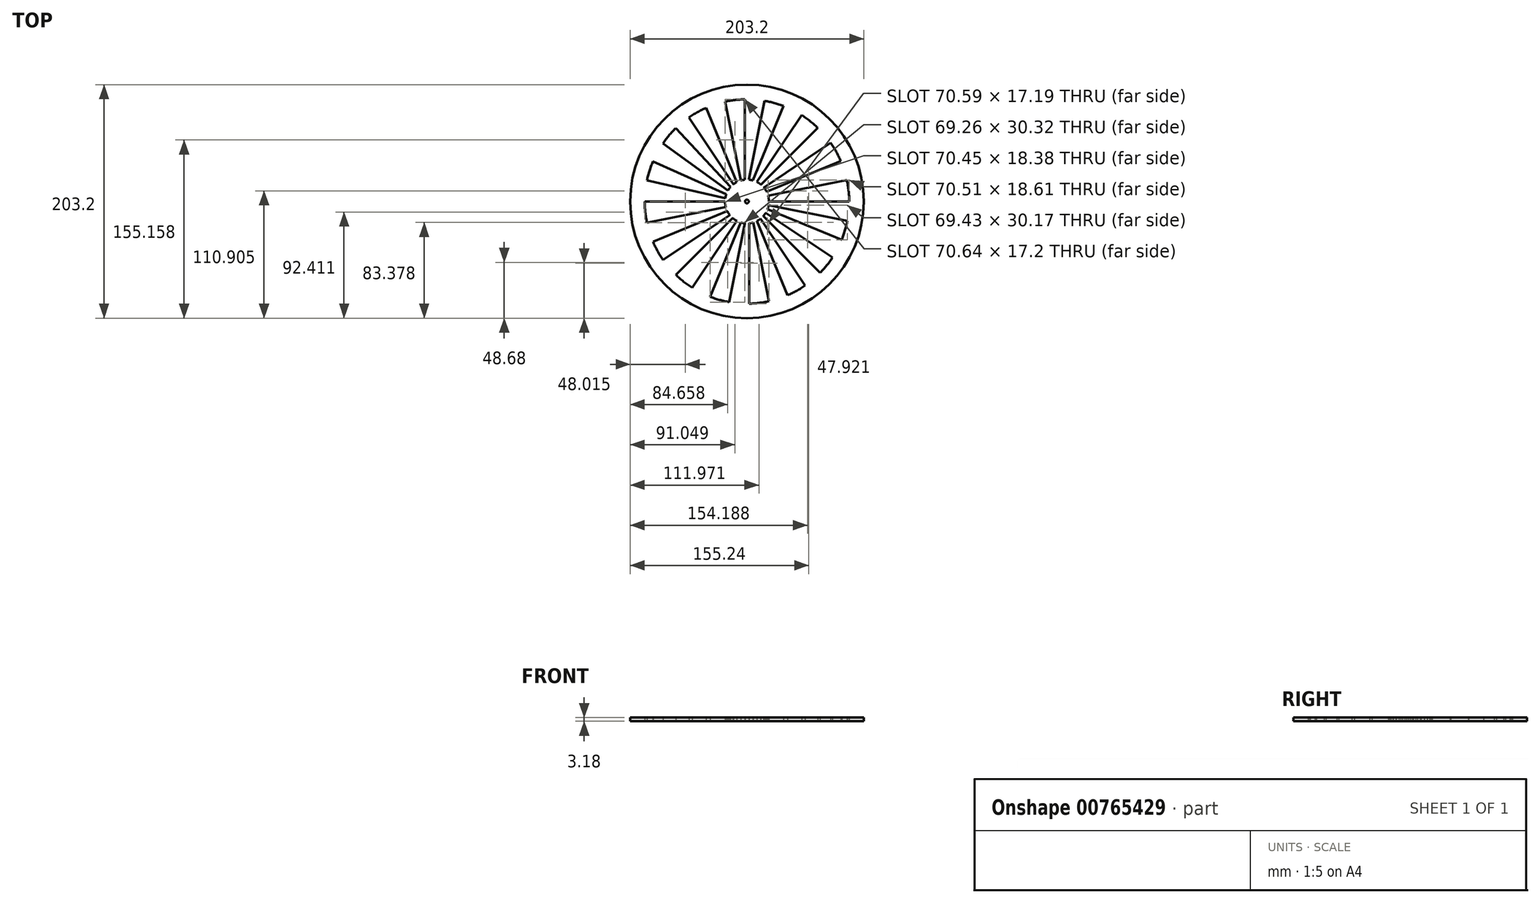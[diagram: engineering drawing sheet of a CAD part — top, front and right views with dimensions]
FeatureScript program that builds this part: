
annotation { "Feature Type Name" : "Feature", "Feature Type Description" : "" }
export const myFeature = defineFeature(function(context is Context, id is Id, definition is map)
    precondition{}
    {
        {
            var Q0;
            Q0=qCreatedBy(makeId("Top.planeOp"),FACE);
            var sketch = newSketch(context, id + "F0", { "sketchPlane" : qUnion([Q0])});
            skCircle(sketch, "E0", {"center": v(-222.01, 0) * mm, "radius": 101.6 * mm});
            skCircle(sketch, "E1", {"center": v(-222.01, 0) * mm, "radius": 88.9 * mm});
            skLineSegment(sketch, "E2", {"start": v(-241.06, 0) * mm, "end": v(-310.91, 0) * mm});
            skLineSegment(sketch, "E3", {"start": v(-202.96, 0) * mm, "end": v(-133.11, 0) * mm});
            skCircle(sketch, "E4", {"center": v(-222.01, 0) * mm, "radius": 1.59 * mm});
            skCircle(sketch, "E5", {"center": v(-222.01, 0) * mm, "radius": 19.05 * mm});
            skLineSegment(sketch, "E6", {"start": v(-223.96, 18.95) * mm, "end": v(-223.96, 88.88) * mm});
            skLineSegment(sketch, "E7", {"start": v(-220.24, -18.97) * mm, "end": v(-220.24, -88.88) * mm});
            skLineSegment(sketch, "E8", {"start": v(-283.88, -63.84) * mm, "end": v(-234.46, -14.42) * mm});
            skLineSegment(sketch, "E9", {"start": v(-283.97, 63.76) * mm, "end": v(-236.38, 12.52) * mm});
            skLineSegment(sketch, "E10", {"start": v(-207.77, -12.65) * mm, "end": v(-158.36, -62.06) * mm});
            skLineSegment(sketch, "E11", {"start": v(-239.95, 6.4) * mm, "end": v(-303.85, 34.73) * mm});
            skLineSegment(sketch, "E12", {"start": v(-309.02, 18.27) * mm, "end": v(-240.83, 2.96) * mm});
            skLineSegment(sketch, "E13", {"start": v(-303.72, -35.04) * mm, "end": v(-239.16, -8.3) * mm});
            skLineSegment(sketch, "E14", {"start": v(-309, -18.38) * mm, "end": v(-240.46, -4.75) * mm});
            skLineSegment(sketch, "E15", {"start": v(-236.92, -11.86) * mm, "end": v(-295.04, -50.7) * mm});
            skLineSegment(sketch, "E16", {"start": v(-227.35, -18.29) * mm, "end": v(-254.11, -82.9) * mm});
            skLineSegment(sketch, "E17", {"start": v(-223.8, -18.97) * mm, "end": v(-237.43, -87.55) * mm});
            skLineSegment(sketch, "E18", {"start": v(-230.9, -16.85) * mm, "end": v(-269.76, -75) * mm});
            skLineSegment(sketch, "E19", {"start": v(-216.68, -18.29) * mm, "end": v(-203.04, -86.85) * mm});
            skLineSegment(sketch, "E20", {"start": v(-213.37, -16.98) * mm, "end": v(-186.63, -81.55) * mm});
            skLineSegment(sketch, "E21", {"start": v(-210.37, -15.08) * mm, "end": v(-171.54, -73.18) * mm});
            skLineSegment(sketch, "E22", {"start": v(-204.13, -6.57) * mm, "end": v(-139.6, -33.3) * mm});
            skLineSegment(sketch, "E23", {"start": v(-203.22, -3.14) * mm, "end": v(-134.7, -16.76) * mm});
            skLineSegment(sketch, "E24", {"start": v(-205.67, -9.78) * mm, "end": v(-147.57, -48.6) * mm});
            skLineSegment(sketch, "E25", {"start": v(-204.98, 8.53) * mm, "end": v(-140.41, 35.28) * mm});
            skLineSegment(sketch, "E26", {"start": v(-207.3, 12.09) * mm, "end": v(-149.15, 50.94) * mm});
            skLineSegment(sketch, "E27", {"start": v(-203.63, 4.98) * mm, "end": v(-135.08, 18.61) * mm});
            skLineSegment(sketch, "E28", {"start": v(-190.13, 82.99) * mm, "end": v(-216.9, 18.35) * mm});
            skLineSegment(sketch, "E29", {"start": v(-174.49, 75.13) * mm, "end": v(-213.35, 16.97) * mm});
            skLineSegment(sketch, "E30", {"start": v(-220.4, 18.98) * mm, "end": v(-206.76, 87.58) * mm});
            skLineSegment(sketch, "E31", {"start": v(-230.81, 16.9) * mm, "end": v(-257.56, 81.48) * mm});
            skLineSegment(sketch, "E32", {"start": v(-227.52, 18.24) * mm, "end": v(-241.16, 86.81) * mm});
            skLineSegment(sketch, "E33", {"start": v(-233.8, 14.97) * mm, "end": v(-272.63, 73.08) * mm});
            skLineSegment(sketch, "E34", {"start": v(-238.45, 9.63) * mm, "end": v(-295.11, 50.6) * mm});
            skLineSegment(sketch, "E35", {"start": v(-209.8, 14.61) * mm, "end": v(-160.36, 64.05) * mm});
            skSolve(sketch);
        }
        {
            var Q0;
            {var subQ0=sQuery(id+"F0.wireOp",EDGE,"E10");Q0=makeQuery(id+"F0.imprint","IMPRINT",FACE,{"disambiguationData":[TD([[makeQuery(id+"F0.imprint","IMPRINT",EDGE,{"derivedFrom":subQ0}),-1.0]])]});}
            var Q1;
            {var subQ0=sQuery(id+"F0.wireOp",EDGE,"E19");Q1=makeQuery(id+"F0.imprint","IMPRINT",FACE,{"disambiguationData":[TD([[makeQuery(id+"F0.imprint","IMPRINT",EDGE,{"derivedFrom":subQ0}),1.0]])]});}
            var Q2;
            {var subQ0=sQuery(id+"F0.wireOp",EDGE,"E7");Q2=makeQuery(id+"F0.imprint","IMPRINT",FACE,{"disambiguationData":[TD([[makeQuery(id+"F0.imprint","IMPRINT",EDGE,{"derivedFrom":subQ0}),-1.0]])]});}
            var Q3;
            {var subQ0=sQuery(id+"F0.wireOp",EDGE,"E16");Q3=makeQuery(id+"F0.imprint","IMPRINT",FACE,{"disambiguationData":[TD([[makeQuery(id+"F0.imprint","IMPRINT",EDGE,{"derivedFrom":subQ0}),-1.0]])]});}
            var Q4;
            {var subQ0=sQuery(id+"F0.wireOp",EDGE,"E8");Q4=makeQuery(id+"F0.imprint","IMPRINT",FACE,{"disambiguationData":[TD([[makeQuery(id+"F0.imprint","IMPRINT",EDGE,{"derivedFrom":subQ0}),1.0]])]});}
            var Q5;
            {var subQ0=sQuery(id+"F0.wireOp",EDGE,"E13");Q5=makeQuery(id+"F0.imprint","IMPRINT",FACE,{"disambiguationData":[TD([[makeQuery(id+"F0.imprint","IMPRINT",EDGE,{"derivedFrom":subQ0}),1.0]])]});}
            var Q6;
            {var subQ0=sQuery(id+"F0.wireOp",EDGE,"E2");Q6=makeQuery(id+"F0.imprint","IMPRINT",FACE,{"disambiguationData":[TD([[makeQuery(id+"F0.imprint","IMPRINT",EDGE,{"derivedFrom":subQ0}),-1.0]])]});}
            var Q7;
            Q7=makeQuery(id+"F0.imprint","IMPRINT",FACE,{"disambiguationData":[TD([[makeQuery(id+"F0.imprint","IMPRINT",EDGE,{"derivedFrom":sQuery(id+"F0.wireOp",EDGE,"E0")}),1.0]])]});
            var Q8;
            {var subQ0=sQuery(id+"F0.wireOp",EDGE,"E22");Q8=makeQuery(id+"F0.imprint","IMPRINT",FACE,{"disambiguationData":[TD([[makeQuery(id+"F0.imprint","IMPRINT",EDGE,{"derivedFrom":subQ0}),-1.0]])]});}
            var Q9;
            {var subQ0=sQuery(id+"F0.wireOp",EDGE,"E3");Q9=makeQuery(id+"F0.imprint","IMPRINT",FACE,{"disambiguationData":[TD([[makeQuery(id+"F0.imprint","IMPRINT",EDGE,{"derivedFrom":subQ0}),-1.0]])]});}
            var Q10;
            {var subQ0=sQuery(id+"F0.wireOp",EDGE,"E11");Q10=makeQuery(id+"F0.imprint","IMPRINT",FACE,{"disambiguationData":[TD([[makeQuery(id+"F0.imprint","IMPRINT",EDGE,{"derivedFrom":subQ0}),-1.0]])]});}
            var Q11;
            {var subQ0=sQuery(id+"F0.wireOp",EDGE,"E9");Q11=makeQuery(id+"F0.imprint","IMPRINT",FACE,{"disambiguationData":[TD([[makeQuery(id+"F0.imprint","IMPRINT",EDGE,{"derivedFrom":subQ0}),1.0]])]});}
            var Q12;
            {var subQ0=sQuery(id+"F0.wireOp",EDGE,"E31");Q12=makeQuery(id+"F0.imprint","IMPRINT",FACE,{"disambiguationData":[TD([[makeQuery(id+"F0.imprint","IMPRINT",EDGE,{"derivedFrom":subQ0}),-1.0]])]});}
            var Q13;
            {var subQ0=sQuery(id+"F0.wireOp",EDGE,"E6");Q13=makeQuery(id+"F0.imprint","IMPRINT",FACE,{"disambiguationData":[TD([[makeQuery(id+"F0.imprint","IMPRINT",EDGE,{"derivedFrom":subQ0}),-1.0]])]});}
            var Q14;
            {var subQ0=sQuery(id+"F0.wireOp",EDGE,"E28");Q14=makeQuery(id+"F0.imprint","IMPRINT",FACE,{"disambiguationData":[TD([[makeQuery(id+"F0.imprint","IMPRINT",EDGE,{"derivedFrom":subQ0}),1.0]])]});}
            var Q15;
            {var subQ0=sQuery(id+"F0.wireOp",EDGE,"E26");Q15=makeQuery(id+"F0.imprint","IMPRINT",FACE,{"disambiguationData":[TD([[makeQuery(id+"F0.imprint","IMPRINT",EDGE,{"derivedFrom":subQ0}),1.0]])]});}
            var Q16;
            {var subQ0=sQuery(id+"F0.wireOp",EDGE,"E25");Q16=makeQuery(id+"F0.imprint","IMPRINT",FACE,{"disambiguationData":[TD([[makeQuery(id+"F0.imprint","IMPRINT",EDGE,{"derivedFrom":subQ0}),-1.0]])]});}
            var Q17;
            Q17=makeQuery(id+"F0.imprint","IMPRINT",FACE,{"disambiguationData":[TD([[makeQuery(id+"F0.imprint","IMPRINT",EDGE,{"derivedFrom":sQuery(id+"F0.wireOp",EDGE,"E4")}),-1.0]])]});
            extrude(context, id + "F1", {"entities" : qUnion([Q0, Q1, Q2, Q3, Q4, Q5, Q6, Q7, Q8, Q9, Q10, Q11, Q12, Q13, Q14, Q15, Q16, Q17]), "depth" : 3.17 * mm, "offsetDistance" : 25.4 * mm});
        }
    });
